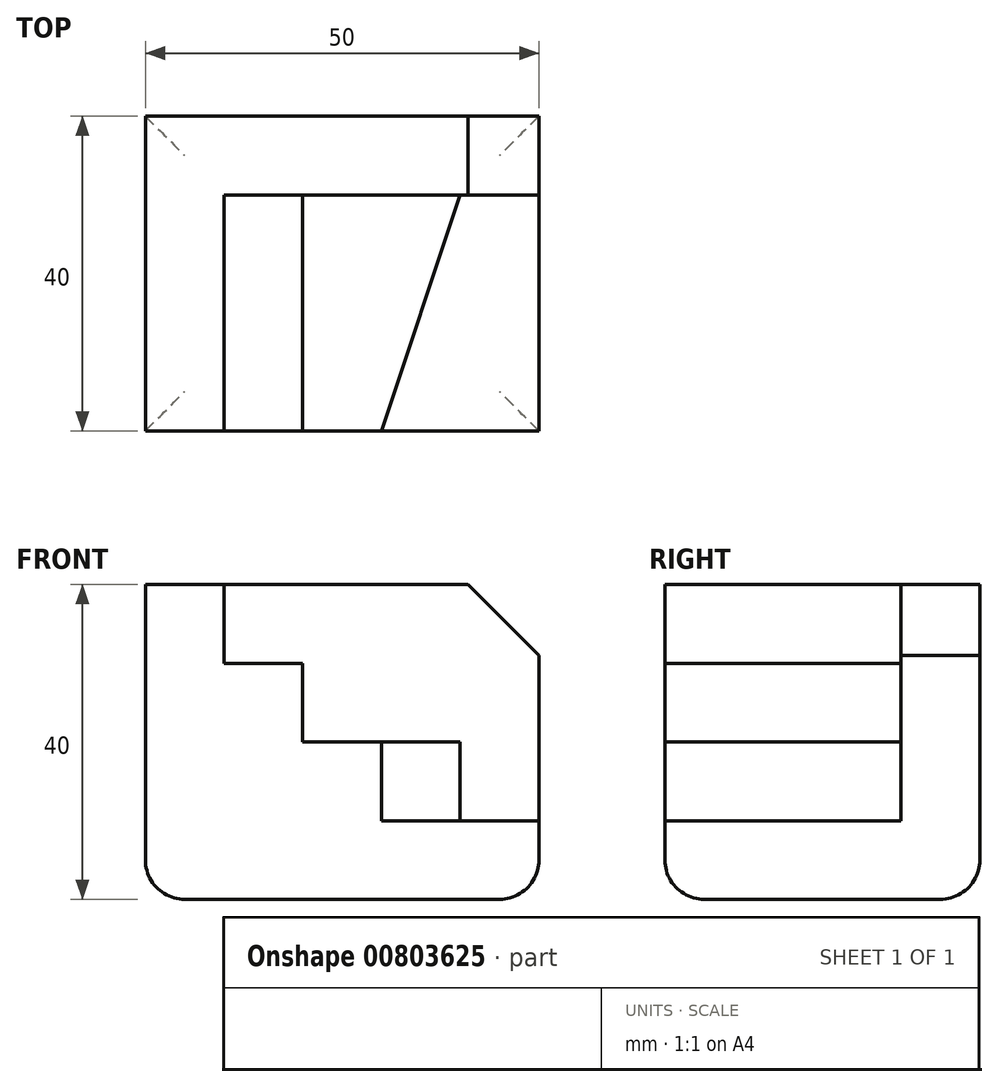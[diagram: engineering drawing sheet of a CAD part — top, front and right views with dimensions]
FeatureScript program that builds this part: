
annotation { "Feature Type Name" : "Feature", "Feature Type Description" : "" }
export const myFeature = defineFeature(function(context is Context, id is Id, definition is map)
    precondition{}
    {
        {
            var Q0;
            Q0=qCreatedBy(makeId("Top.planeOp"),FACE);
            var sketch = newSketch(context, id + "F0", { "sketchPlane" : qUnion([Q0])});
            skLineSegment(sketch, "E0.bottom", {"start": v(0, 0) * mm, "end": v(50, 0) * mm});
            skLineSegment(sketch, "E0.top", {"start": v(0, 40) * mm, "end": v(50, 40) * mm});
            skLineSegment(sketch, "E0.left", {"start": v(0, 0) * mm, "end": v(0, 40) * mm});
            skLineSegment(sketch, "E0.right", {"start": v(50, 0) * mm, "end": v(50, 40) * mm});
            skLineSegment(sketch, "E1", {"start": v(10, 0) * mm, "end": v(10, 30) * mm});
            skLineSegment(sketch, "E2", {"start": v(10, 30) * mm, "end": v(50, 30) * mm});
            skLineSegment(sketch, "E3", {"start": v(20, 0) * mm, "end": v(20, 30) * mm});
            skLineSegment(sketch, "E4", {"start": v(30, 0) * mm, "end": v(40, 30) * mm});
            skSolve(sketch);
        }
        {
            var Q0;
            {var subQ1=sQuery(id+"F0.wireOp",EDGE,"E0.top");Q0=makeQuery(id+"F0.imprint","IMPRINT",FACE,{"disambiguationData":[TD([[makeQuery(id+"F0.imprint","IMPRINT",EDGE,{"derivedFrom":subQ1}),-1.0]])]});}
            extrude(context, id + "F1", {"entities" : qUnion([Q0]), "depth" : 40 * mm, "offsetDistance" : 25 * mm});
        }
        {
            var Q0;
            {var subQ0=sQuery(id+"F0.wireOp",EDGE,"E1");Q0=makeQuery(id+"F0.imprint","IMPRINT",FACE,{"disambiguationData":[TD([[makeQuery(id+"F0.imprint","IMPRINT",EDGE,{"derivedFrom":subQ0}),-1.0]])]});}
            extrude(context, id + "F2", {"entities" : qUnion([Q0]), "operationType" : NewBodyOperationType.ADD, "depth" : 30 * mm, "offsetDistance" : 25 * mm});
        }
        {
            var Q0;
            {var subQ0=sQuery(id+"F0.wireOp",EDGE,"E3");Q0=makeQuery(id+"F0.imprint","IMPRINT",FACE,{"disambiguationData":[TD([[makeQuery(id+"F0.imprint","IMPRINT",EDGE,{"derivedFrom":subQ0}),-1.0]])]});}
            extrude(context, id + "F3", {"entities" : qUnion([Q0]), "operationType" : NewBodyOperationType.ADD, "depth" : 20 * mm, "offsetDistance" : 25 * mm});
        }
        {
            var Q0;
            {var subQ3=sQuery(id+"F0.wireOp",EDGE,"E4");Q0=makeQuery(id+"F0.imprint","IMPRINT",FACE,{"disambiguationData":[TD([[makeQuery(id+"F0.imprint","IMPRINT",EDGE,{"derivedFrom":subQ3}),-1.0]])]});}
            extrude(context, id + "F4", {"entities" : qUnion([Q0]), "operationType" : NewBodyOperationType.ADD, "depth" : 10 * mm, "offsetDistance" : 25 * mm});
        }
        {
            var Q0;
            Q0=makeQuery(id+"F1.opExtrude","CAP_EDGE",EDGE,{"disambiguationData":[OSD([sQuery(id+"F0.wireOp",EDGE,"E0.right")])],"isStart":false});
            chamfer(context, id + "F5", {"entities" : qUnion([Q0]), "width" : 9 * mm, "tangentPropagation" : true});
        }
        {
            var Q0;
            {var subQ0=sQuery(id+"F0.wireOp",EDGE,"E0.right");Q0=makeQuery(id+"F4.boolean.opBoolean","MERGE",EDGE,{"derivedFrom":[makeQuery(id+"F1.opExtrude","CAP_EDGE",EDGE,{"disambiguationData":[OSD([subQ0])],"isStart":true}),makeQuery(id+"F4.opExtrude","CAP_EDGE",EDGE,{"disambiguationData":[OSD([subQ0])],"isStart":true})]});}
            var Q1;
            {var subQ0=sQuery(id+"F0.wireOp",EDGE,"E0.bottom");Q1=makeQuery(id+"F4.boolean.opBoolean","MERGE",EDGE,{"derivedFrom":[makeQuery(id+"F3.boolean.opBoolean","MERGE",EDGE,{"derivedFrom":[makeQuery(id+"F2.boolean.opBoolean","MERGE",EDGE,{"derivedFrom":[makeQuery(id+"F1.opExtrude","CAP_EDGE",EDGE,{"disambiguationData":[OSD([subQ0])],"isStart":true}),makeQuery(id+"F2.opExtrude","CAP_EDGE",EDGE,{"disambiguationData":[OSD([subQ0])],"isStart":true})]}),makeQuery(id+"F3.opExtrude","CAP_EDGE",EDGE,{"disambiguationData":[OSD([subQ0])],"isStart":true})]}),makeQuery(id+"F4.opExtrude","CAP_EDGE",EDGE,{"disambiguationData":[OSD([subQ0])],"isStart":true})]});}
            var Q2;
            Q2=makeQuery(id+"F1.opExtrude","CAP_EDGE",EDGE,{"disambiguationData":[OSD([sQuery(id+"F0.wireOp",EDGE,"E0.left")])],"isStart":true});
            var Q3;
            Q3=makeQuery(id+"F1.opExtrude","CAP_EDGE",EDGE,{"disambiguationData":[OSD([sQuery(id+"F0.wireOp",EDGE,"E0.top")])],"isStart":true});
            fillet(context, id + "F6", {"entities" : qUnion([Q0, Q1, Q2, Q3]), "radius" : 5 * mm, "tangentPropagation" : true, "allowEdgeOverflow" : false});
        }
    });
